# Revit family: АРМ тип 7-L_RV17_LOD_400
name_source: partatom
category: Электрооборудование
revit_build: Autodesk Revit 2017 (Build: 20170118_1100(x64)
units: mm (PartAtom-declared; Revit-internal decimal feet)

## family parameters
Всегда вертикально = Да
Конфигурация панели = Два столбца, слева направо
На основе рабочей плоскости = Нет
Общий = Нет
При загрузке вырезать с полостями = Нет
Размер круглого соединителя = Использовать диаметр
Тип детали = Щит
Точка расчета площади = Нет

## types (1)
- АРМ тип 7-L
    ADSK_URL страницы изделия = https://stilsoft.ru
    ADSK_Единица измерения = шт.
    ADSK_Завод-изготовитель = ООО «Основа Безопасности»
    ADSK_Количество = 0
    ADSK_Марка = СТВФ.426484.163
    ADSK_Масса = 0
    ADSK_Наименование = АРМ тип 7-L
    ADSK_Размер_Высота = 420 мм
    ADSK_Размер_Глубина = 220 мм
    ADSK_Размер_Ширина = 551 мм
    Габаритные размеры (мм) - монитора с подставкой = 551×420×220
    Габаритные размеры (мм) -процессорного модуля = 90×234×222
    Диагональ монитора, дюйм = 24
    Диапазон рабочих температур, °С = от +5 до +50
    Количество мониторов, шт. = 1
    Мощность = 95
    Напряжение = 220
    Объем накопителя, ГБ = 500
    Разрешение экрана, пикс. = 1920 x 1080
    Сетевая карта с базовой скоростью передачи данных, Мбит/с = 1000
    Установленное ПО (1) = ОС "Astra Linux Common Edition"
    Установленное ПО (2) = Антивирус Касперского
    Установленное ПО (3) = Базовое серверное ПО «Синергет»
